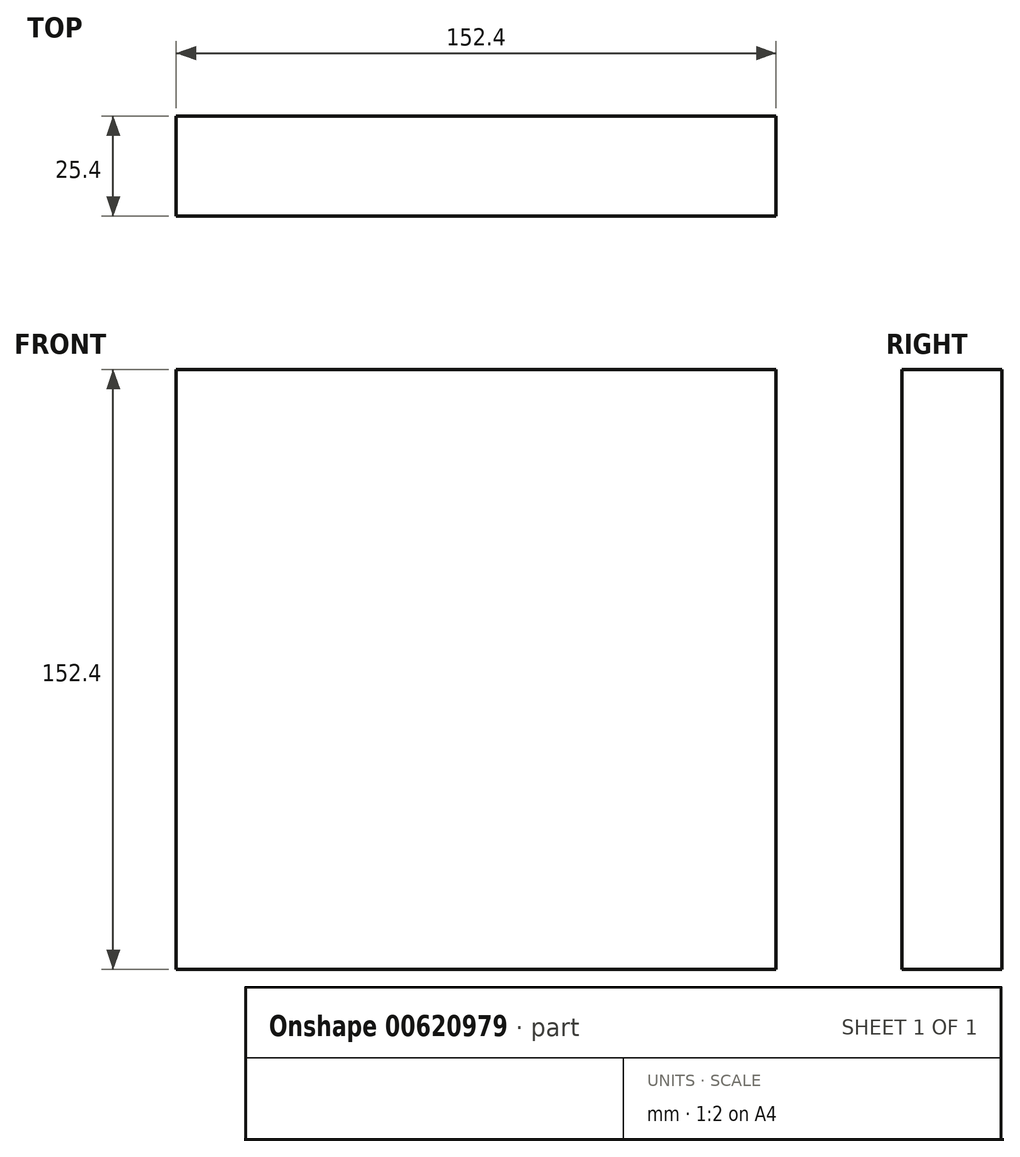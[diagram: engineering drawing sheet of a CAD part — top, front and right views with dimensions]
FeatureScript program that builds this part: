
annotation { "Feature Type Name" : "Feature", "Feature Type Description" : "" }
export const myFeature = defineFeature(function(context is Context, id is Id, definition is map)
    precondition{}
    {
        {
            var Q0;
            Q0=qCreatedBy(makeId("Front.planeOp"),FACE);
            var sketch = newSketch(context, id + "F0", { "sketchPlane" : qUnion([Q0])});
            skLineSegment(sketch, "E0.bottom", {"start": v(-76.2, -76.2) * mm, "end": v(76.2, -76.2) * mm});
            skLineSegment(sketch, "E0.top", {"start": v(-76.2, 76.2) * mm, "end": v(76.2, 76.2) * mm});
            skLineSegment(sketch, "E0.left", {"start": v(-76.2, -76.2) * mm, "end": v(-76.2, 76.2) * mm});
            skLineSegment(sketch, "E0.right", {"start": v(76.2, -76.2) * mm, "end": v(76.2, 76.2) * mm});
            skPoint(sketch, "E0.middle", {"position": v(0, 0) * mm});
            skSolve(sketch);
        }
        {
            var Q0;
            Q0 = qSketchRegion(id + "F0", true);
            extrude(context, id + "F1", {"entities" : qUnion([Q0]), "depth" : 25.4 * mm, "offsetDistance" : 25.4 * mm});
        }
    });
